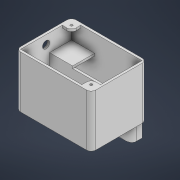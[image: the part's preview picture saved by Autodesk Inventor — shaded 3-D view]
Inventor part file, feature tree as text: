
AUTODESK INVENTOR PART (.ipt)
format: ipt  version: 2022 (Build 260153000, 153)  size: 227,840 bytes
history: native  units: in
note: dims shown in document units (in); Inventor stores cm internally (conversion verified against a paired STEP export)
features: extrude x12, sketch x12, fillet x8, shell x1
ambient origin geometry x8: Origin, YZ Plane, XZ Plane, XY Plane, X Axis, Y Axis, Z Axis, Center Point
bodies: Solid1 (feature_tree)
feature tree (33):
  extrude  "Extrusion1"  Depth=1.7717in
  shell  "Shell1"  Thickness=1.8898in
  extrude  "Extrusion2"  Depth=1.1811in
  extrude  "Extrusion3"  Depth=2.4016in
  fillet  "Fillet1"  [1 undecoded]
  fillet  "Fillet2"  Radius=1.7323in
  fillet  "Fillet3"  Radius=0.0787in
  fillet  "Fillet4"  Radius=1.0236in
  extrude  "Extrusion4"  Depth=0.1575in
  extrude  "Extrusion5"  Depth=0.1575in
  extrude  "Extrusion7"  Depth=0.7874in TaperAngle=0.0deg
  fillet  "Fillet6"  Radius=0.3937in
  extrude  "Extrusion10"  Depth=0.0787in
  extrude  "Extrusion11"  Depth=0.0787in TaperAngle=0.0deg
  fillet  "Fillet7"  Radius=0.1575in
  extrude  "Extrusion12"  Depth=0.0787in
  fillet  "Fillet8"  Radius=0.315in
  extrude  "Extrusion13"  Depth=0.1575in
  fillet  "Fillet9"  Radius=0.5906in
  extrude  "Extrusion14"  Depth=0.5906in TaperAngle=0.0deg
  extrude  "Extrusion15"  TaperAngle=0.0deg  [1 undecoded]
  sketch  "Sketch1"  dims[d3=2.5591in d4=1.7717in d5=1.8898in d6=0.0in]
  sketch  "Sketch2"  dims[d7=0.0787in d9=1.1811in]
  sketch  "Sketch3"  dims[d10=0.3937in d11=2.4016in d12=0.0in d13=0.0in d16=1.7323in d17=0.0787in d18=1.0236in d19=0.0in]
  sketch  "Sketch4"  dims[d20=0.1575in d21=0.1575in]
  sketch  "Sketch8"  dims[d22=0.1575in d23=0.1575in]
  sketch  "Sketch10"  dims[d24=0.0787in d25=0.7874in d26=0.0in d27=0.3937in]
  sketch  "Sketch13"  dims[d28=0.315in d29=0.0787in]
  sketch  "Sketch14"  dims[d30=0.315in d31=0.0in d38=0.0787in d39=0.0in d50=0.1575in]
  sketch  "Sketch15"  dims[d51=0.315in d52=0.0787in d53=0.315in d54=0.0in]
  sketch  "Sketch16"  dims[d58=0.0787in d59=0.0in d60=0.1575in d62=0.5906in d63=0.0in]
  sketch  "Sketch17"  dims[d64=0.3937in d68=0.5906in d69=0.0in]
  sketch  "Sketch19"  dims[d70=0.2756in d74=0.0in d75=0.0in d78=0.2461in d79=0.0in d80=0.0in d65=0.0in d66=0.0in d67=0.0in d71=0.0394in d72=0.0394in d73=0.0059in d76=0.5635in d77=0.0295in d81=0.0148in]
note: 2 required parameter values undecoded (feature->parameter linkage not recoverable at this tier; creation-order binding heuristic only, values carry confidence <= 0.55)
